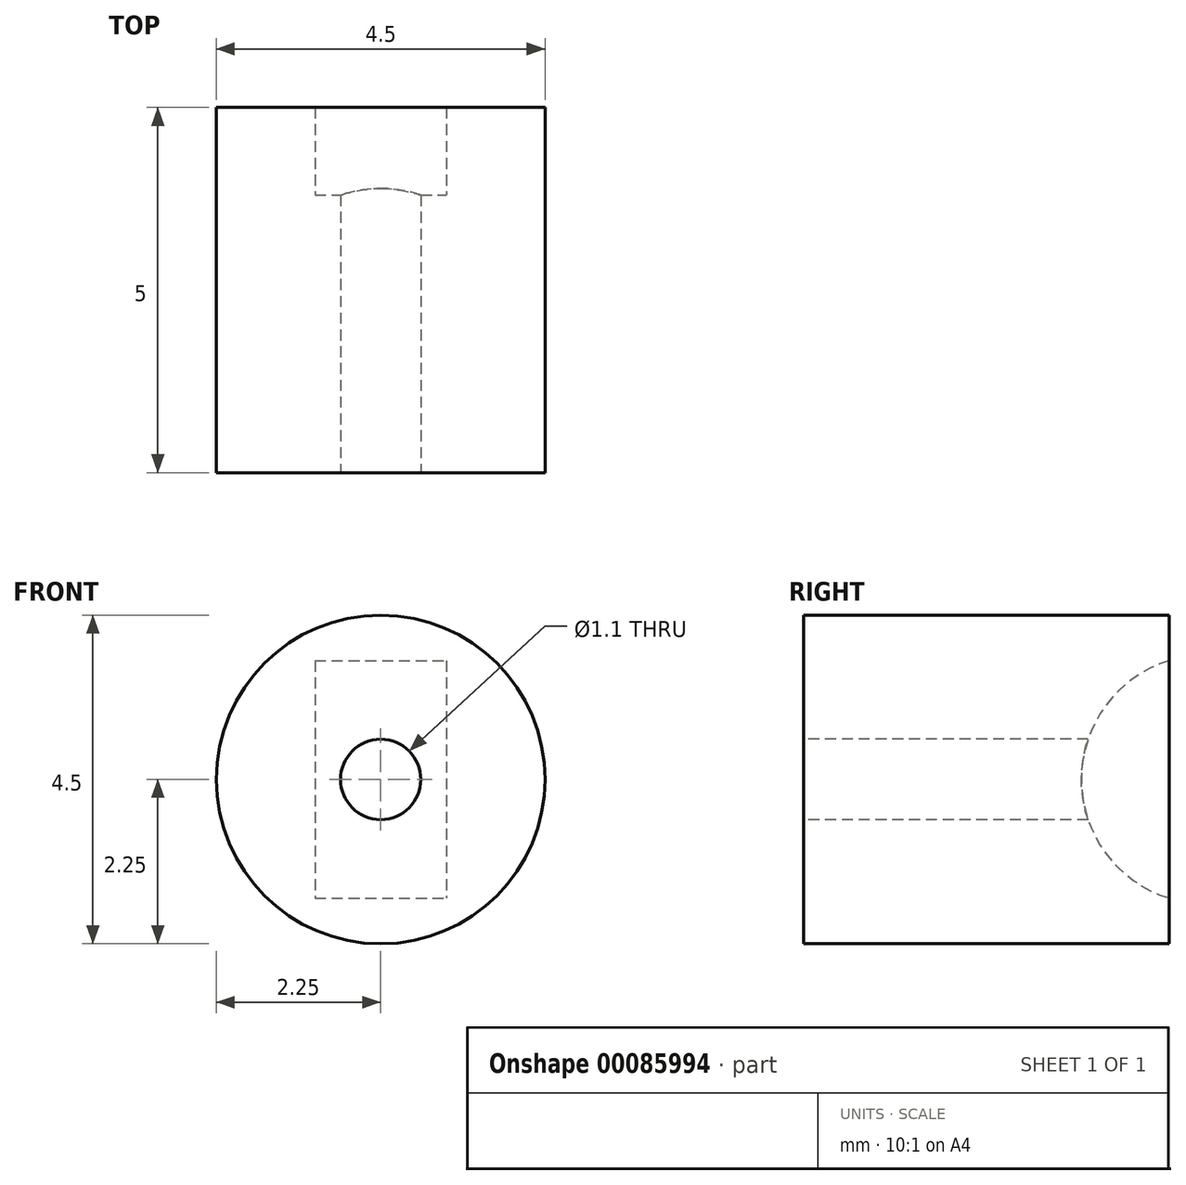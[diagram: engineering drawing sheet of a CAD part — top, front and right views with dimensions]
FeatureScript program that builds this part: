
annotation { "Feature Type Name" : "Feature", "Feature Type Description" : "" }
export const myFeature = defineFeature(function(context is Context, id is Id, definition is map)
    precondition{}
    {
        {
            var Q0;
            Q0=qCreatedBy(makeId("Right.planeOp"),FACE);
            var sketch = newSketch(context, id + "F0", { "sketchPlane" : qUnion([Q0])});
            skLineSegment(sketch, "E0", {"start": v(0, 0.55) * mm, "end": v(0, 2.25) * mm});
            skLineSegment(sketch, "E1", {"start": v(0, 2.25) * mm, "end": v(5, 2.25) * mm});
            skLineSegment(sketch, "E2", {"start": v(5, 2.25) * mm, "end": v(5, 0) * mm});
            skLineSegment(sketch, "E3", {"start": v(5, 0) * mm, "end": v(4, 0) * mm});
            skLineSegment(sketch, "E4", {"start": v(4, 0) * mm, "end": v(4, 0.55) * mm});
            skLineSegment(sketch, "E5", {"start": v(4, 0.55) * mm, "end": v(0, 0.55) * mm});
            skLineSegment(sketch, "E6", {"start": v(-1.7, 0) * mm, "end": v(6.4, 0) * mm, "construction": true});
            skSolve(sketch);
        }
        {
            var Q0;
            Q0 = qSketchRegion(id + "F0", true);
            var Q1;
            Q1=sQuery(id+"F0.wireOp",EDGE,"E6");
            revolve(context, id + "F1", {"entities" : qUnion([Q0]), "axis" : qUnion([Q1]), "revolveType" : RevolveType.FULL});
        }
        {
            var Q0;
            Q0=qCreatedBy(makeId("Right.planeOp"),FACE);
            var sketch = newSketch(context, id + "F2", { "sketchPlane" : qUnion([Q0])});
            skCircle(sketch, "E7", {"center": v(5.5, 0) * mm, "radius": 1.7 * mm});
            skCircle(sketch, "E8", {"center": v(5.5, 0) * mm, "radius": 0.79 * mm, "construction": true});
            skSolve(sketch);
        }
        {
            var Q0;
            Q0 = qSketchRegion(id + "F2", true);
            extrude(context, id + "F3", {"entities" : qUnion([Q0]), "operationType" : NewBodyOperationType.REMOVE, "endBound" : BoundingType.SYMMETRIC, "oppositeDirection" : true, "depth" : 1.8 * mm});
        }
    });
